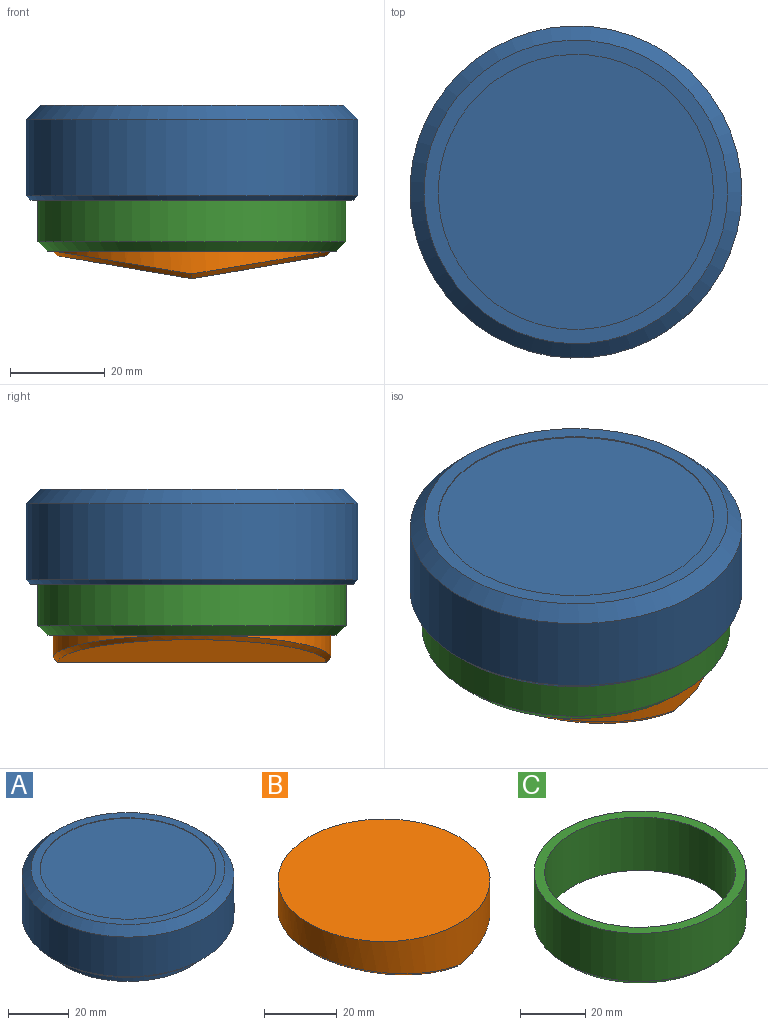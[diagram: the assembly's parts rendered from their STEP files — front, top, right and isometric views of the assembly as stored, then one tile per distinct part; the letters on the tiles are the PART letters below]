
ASSEMBLY  parts=3 mates=2
PART A: 11 faces, bbox 70x70x25 mm
  f0: cylinder r=35mm len=70mm, axis (0,0,-1), area 3518.6mm2, adj f3,f4
  f1: plane 64x64mm, normal (0,0,1), area 574.9mm2, adj f3,f9
  f2: plane 68x68mm, normal (0,0,-1), area 313.4mm2, adj f4,f5
  f3: cone r=32mm half-angle=45deg, axis (0,0,-1), area 893mm2, adj f0,f1
  f4: cone r=35mm half-angle=45deg, axis (0,0,1), area 306.6mm2, adj f0,f2
  f5: cylinder r=32.5mm len=65mm, axis (0,0,-1), area 3063.1mm2, adj f2,f6
  f6: plane 65x65mm, normal (0,0,-1), area 630.5mm2, adj f5,f7
  f7: cylinder r=29.25mm len=58.5mm, axis (0,0,1), area 3675.7mm2, adj f6,f8
  f8: plane 58.5x58.5mm, normal (0,0,-1), area 2687.8mm2, adj f7
  f9: cylinder r=29mm len=58mm, axis (0,0,1), area 41.9mm2, adj f1,f10
  f10: plane 58x58mm, normal (0,0,1), area 2642.1mm2, adj f9
PART B: 7 faces, bbox 58.5x59.1x15.8 mm
  f0: cylinder r=29.25mm len=58.5mm, axis (0,0,-1), area 2570.3mm2, adj f1,f4,f5
  f1: plane 58.5x58.5mm, normal (0,0,1), area 2687.8mm2, adj f0
  f2: plane 56.54x28.15mm, normal (-0.17,0,-0.99), area 1261.9mm2, adj f4,f6
  f3: plane 56.54x28.15mm, normal (0.17,0,-0.99), area 1261.9mm2, adj f5,f6
  f4: bspline ~59.1x34.02mm, area 121.7mm2, adj f0,f2,f5,f6
  f5: bspline ~59.1x34.02mm, area 121.8mm2, adj f0,f3,f4,f6
  f6: cylinder r=2mm len=56.55mm, axis (0,1,0), area 38.3mm2, adj f2,f3,f4,f5
PART C: 5 faces, bbox 65x65x20 mm
  f0: cylinder r=32.5mm len=65mm, axis (0,0,1), area 3675.7mm2, adj f2,f4
  f1: plane 61x61mm, normal (0,0,-1), area 234.6mm2, adj f3,f4
  f2: plane 65x65mm, normal (0,0,1), area 630.5mm2, adj f0,f3
  f3: cylinder r=29.25mm len=58.5mm, axis (0,0,1), area 3675.7mm2, adj f1,f2
  f4: cone r=32.5mm half-angle=45deg, axis (0,0,1), area 559.8mm2, adj f0,f1
PLACE A rot(axis=(-0.46,0.7,0.55),0deg) t=(-26.25,-29.58,39.77)mm
PLACE B rot(axis=(-0.46,0.7,0.55),0deg) t=(-26.25,-29.58,28.22)mm
PLACE C rot(axis=(-0.46,0.7,0.55),0deg) t=(-26.25,-29.58,49.06)mm
MATE slider C.f0 <-> A.f9  axis (0,0,1) through (-26.25,-29.58,49.06)mm
MATE slider B.f0 <-> C.f0  axis (0,0,1) through (-26.25,-29.58,38.22)mm
